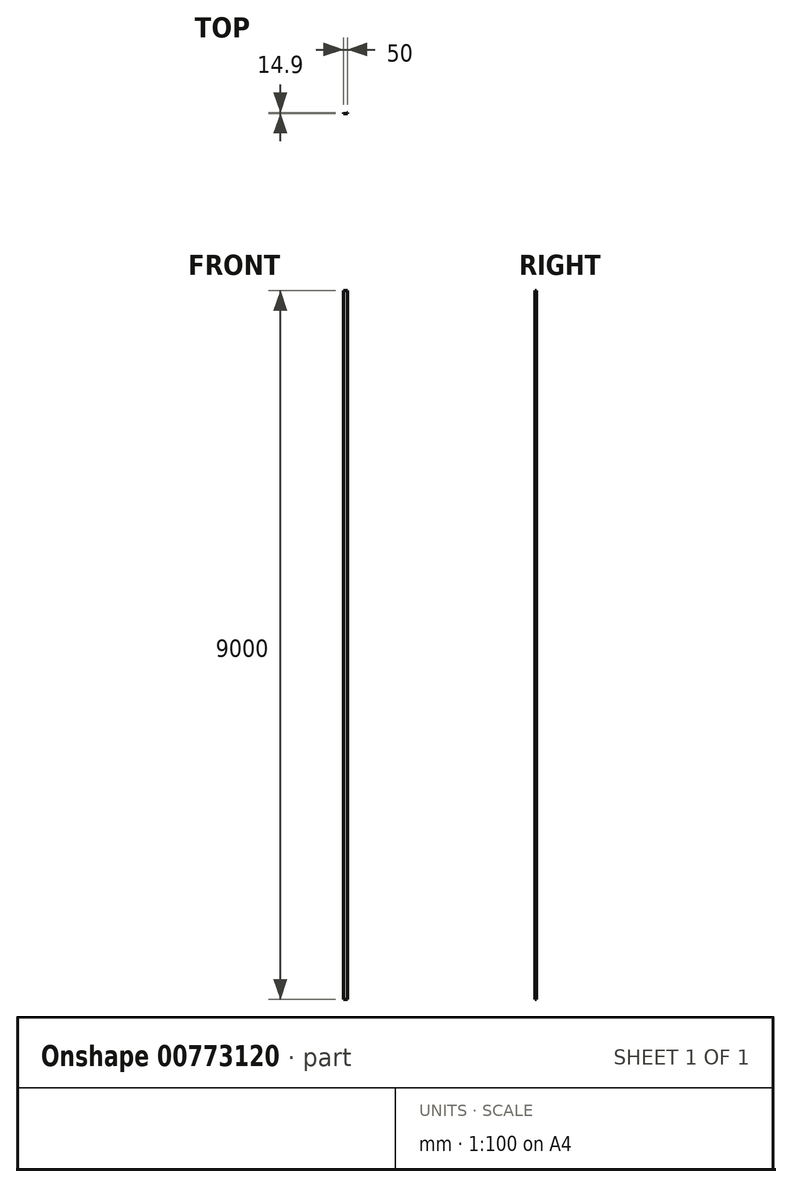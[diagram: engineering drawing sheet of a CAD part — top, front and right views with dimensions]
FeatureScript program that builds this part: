
annotation { "Feature Type Name" : "Feature", "Feature Type Description" : "" }
export const myFeature = defineFeature(function(context is Context, id is Id, definition is map)
    precondition{}
    {
        {
            var Q0;
            Q0=qCreatedBy(makeId("Top.planeOp"),FACE);
            var sketch = newSketch(context, id + "F0", { "sketchPlane" : qUnion([Q0])});
            skLineSegment(sketch, "E0", {"start": v(-25, -6.67) * mm, "end": v(-25, -21.57) * mm});
            skLineSegment(sketch, "E1", {"start": v(-25, -21.57) * mm, "end": v(0, -21.57) * mm});
            skLineSegment(sketch, "E2", {"start": v(-25, -6.67) * mm, "end": v(-23.4, -6.67) * mm});
            skLineSegment(sketch, "E3", {"start": v(-23.4, -6.67) * mm, "end": v(-23.4, -19.97) * mm});
            skLineSegment(sketch, "E4", {"start": v(-23.4, -19.97) * mm, "end": v(0, -19.97) * mm});
            skLineSegment(sketch, "E5", {"start": v(0, 24.5) * mm, "end": v(0, -40.2) * mm, "construction": true});
            skLineSegment(sketch, "E6.MirrorCS", {"start": v(25, -6.67) * mm, "end": v(25, -21.57) * mm});
            skLineSegment(sketch, "E7.MirrorCS", {"start": v(23.4, -19.97) * mm, "end": v(0, -19.97) * mm});
            skLineSegment(sketch, "E8.MirrorCS", {"start": v(25, -21.57) * mm, "end": v(0, -21.57) * mm});
            skLineSegment(sketch, "E9.MirrorCS", {"start": v(25, -6.67) * mm, "end": v(23.4, -6.67) * mm});
            skLineSegment(sketch, "E10.MirrorCS", {"start": v(23.4, -6.67) * mm, "end": v(23.4, -19.97) * mm});
            skSolve(sketch);
        }
        {
            var Q0;
            Q0 = qSketchRegion(id + "F0", true);
            extrude(context, id + "F1", {"entities" : qUnion([Q0]), "depth" : 9000 * mm, "offsetDistance" : 25 * mm});
        }
    });
